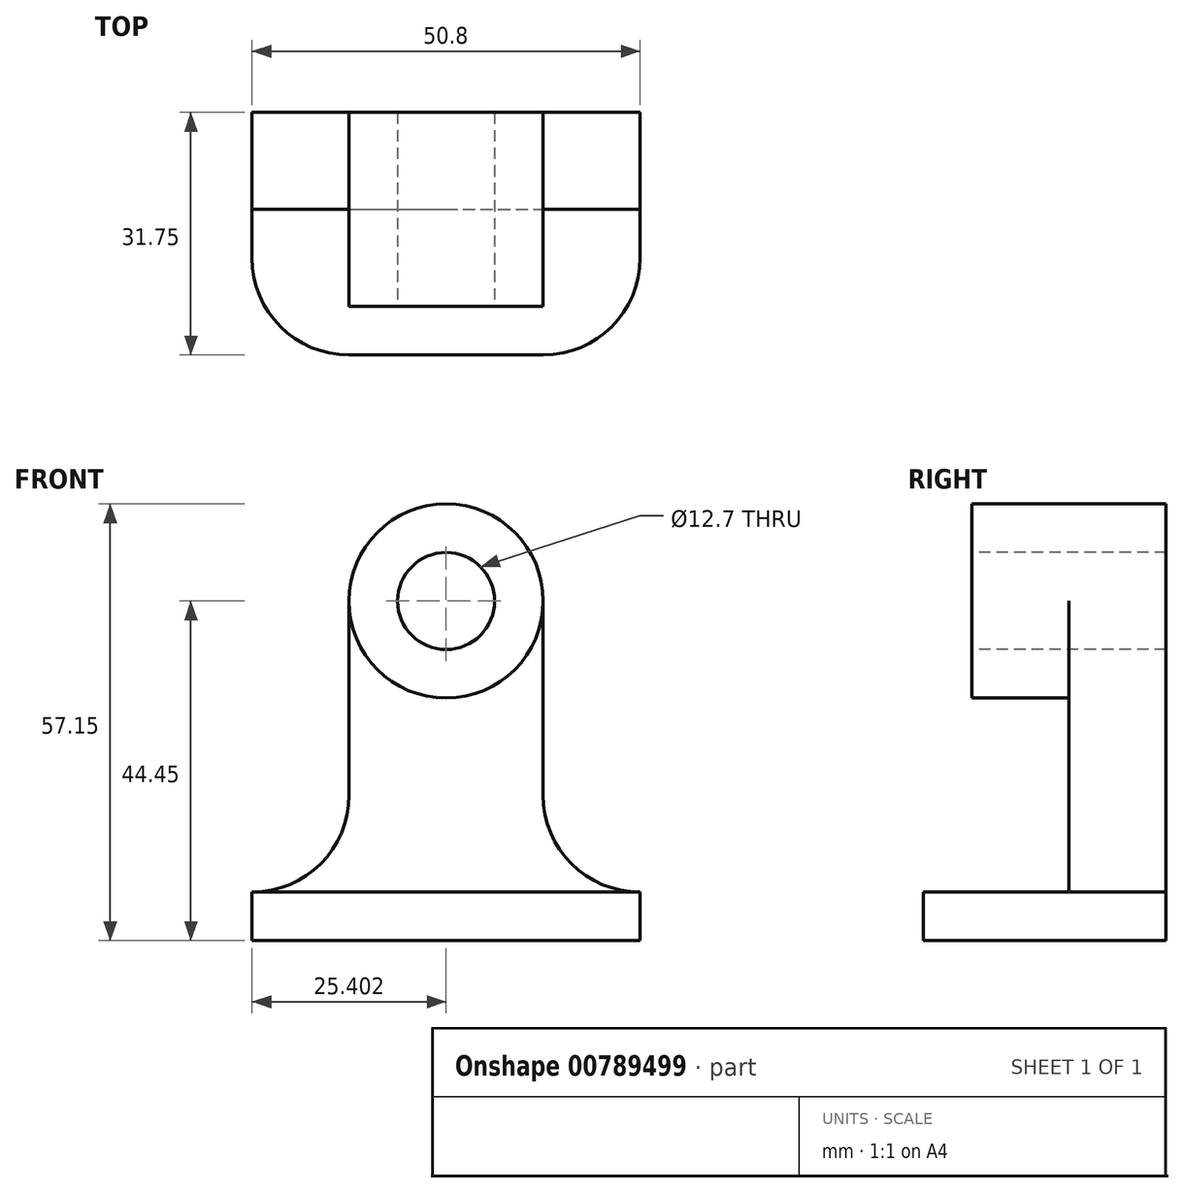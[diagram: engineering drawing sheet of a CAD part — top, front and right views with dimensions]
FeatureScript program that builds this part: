
annotation { "Feature Type Name" : "Feature", "Feature Type Description" : "" }
export const myFeature = defineFeature(function(context is Context, id is Id, definition is map)
    precondition{}
    {
        {
            var Q0;
            Q0=qCreatedBy(makeId("Front.planeOp"),FACE);
            var sketch = newSketch(context, id + "F0", { "sketchPlane" : qUnion([Q0])});
            skLineSegment(sketch, "E0", {"start": v(-22.4, 6.35) * mm, "end": v(-22.4, 0) * mm});
            skLineSegment(sketch, "E1", {"start": v(-22.4, 0) * mm, "end": v(28.4, 0) * mm});
            skLineSegment(sketch, "E2", {"start": v(28.4, 0) * mm, "end": v(28.4, 6.35) * mm});
            skLineSegment(sketch, "E3", {"start": v(28.4, 6.35) * mm, "end": v(15.7, 6.35) * mm});
            skLineSegment(sketch, "E4", {"start": v(-22.4, 6.35) * mm, "end": v(-9.7, 6.35) * mm});
            skLineSegment(sketch, "E5", {"start": v(-9.7, 6.35) * mm, "end": v(-9.7, 57.15) * mm});
            skLineSegment(sketch, "E6", {"start": v(15.7, 6.35) * mm, "end": v(15.7, 57.15) * mm});
            skLineSegment(sketch, "E7", {"start": v(15.7, 57.15) * mm, "end": v(-9.7, 57.15) * mm});
            skSolve(sketch);
        }
        {
            var Q0;
            Q0=makeQuery(id+"F0.imprint","IMPRINT",FACE,{"disambiguationData":[TD([[makeQuery(id+"F0.imprint","IMPRINT",EDGE,{"derivedFrom":sQuery(id+"F0.wireOp",EDGE,"E0")}),1.0]])]});
            extrude(context, id + "F1", {"entities" : qUnion([Q0]), "depth" : 31.75 * mm, "offsetDistance" : 25.4 * mm});
        }
        {
            var Q0;
            Q0=makeQuery(id+"F1.opExtrude","CAP_FACE",FACE,{"disambiguationData":[OSD([sQuery(id+"F0.wireOp",EDGE,"E0"),sQuery(id+"F0.wireOp",EDGE,"E1"),sQuery(id+"F0.wireOp",EDGE,"E2"),sQuery(id+"F0.wireOp",EDGE,"E3"),sQuery(id+"F0.wireOp",EDGE,"E4"),sQuery(id+"F0.wireOp",EDGE,"E5"),sQuery(id+"F0.wireOp",EDGE,"E6"),sQuery(id+"F0.wireOp",EDGE,"E7")])],"isStart":false});
            var sketch = newSketch(context, id + "F2", { "sketchPlane" : qUnion([Q0])});
            skCircle(sketch, "E8", {"center": v(3, 44.45) * mm, "radius": 6.35 * mm});
            skSolve(sketch);
        }
        {
            var Q0;
            Q0=makeQuery(id+"F2.imprint","IMPRINT",FACE,{"disambiguationData":[TD([[makeQuery(id+"F2.imprint","IMPRINT",EDGE,{"derivedFrom":sQuery(id+"F2.wireOp",EDGE,"E8")}),1.0]])]});
            var Q1;
            Q1 = qSketchRegion(id + "F4", true);
            extrude(context, id + "F3", {"entities" : qUnion([Q0, Q1]), "operationType" : NewBodyOperationType.REMOVE, "oppositeDirection" : true, "depth" : 31.75 * mm, "offsetDistance" : 25.4 * mm});
        }
        {
            var Q0;
            Q0=makeQuery(id+"F1.opExtrude","CAP_FACE",FACE,{"disambiguationData":[OSD([sQuery(id+"F0.wireOp",EDGE,"E0"),sQuery(id+"F0.wireOp",EDGE,"E1"),sQuery(id+"F0.wireOp",EDGE,"E2"),sQuery(id+"F0.wireOp",EDGE,"E3"),sQuery(id+"F0.wireOp",EDGE,"E4"),sQuery(id+"F0.wireOp",EDGE,"E5"),sQuery(id+"F0.wireOp",EDGE,"E6"),sQuery(id+"F0.wireOp",EDGE,"E7")])],"isStart":false});
            var sketch = newSketch(context, id + "F4", { "sketchPlane" : qUnion([Q0])});
            skCircle(sketch, "E9", {"center": v(3, 44.45) * mm, "radius": 12.7 * mm});
            skSolve(sketch);
        }
        {
            var Q0;
            {var subQ0=sQuery(id+"F4.wireOp",EDGE,"E9");var subQ1=makeQuery(id+"F1.opExtrude","CAP_EDGE",EDGE,{"disambiguationData":[OSD([sQuery(id+"F0.wireOp",EDGE,"E7")])],"isStart":false});var subQ2=makeQuery(id+"F4.imprint","INTERSECT",VERTEX,{"derivedFrom":[subQ1,subQ0]});Q0=makeQuery(id+"F4.imprint","IMPRINT",FACE,{"disambiguationData":[TD([[makeQuery(id+"F4.imprint","IMPRINT",EDGE,{"disambiguationData":[TD([[subQ2,-1.0]])],"derivedFrom":subQ0}),-1.0]])]});}
            var Q1;
            {var subQ0=sQuery(id+"F4.wireOp",EDGE,"E9");var subQ1=makeQuery(id+"F1.opExtrude","CAP_EDGE",EDGE,{"disambiguationData":[OSD([sQuery(id+"F0.wireOp",EDGE,"E7")])],"isStart":false});var subQ2=makeQuery(id+"F4.imprint","INTERSECT",VERTEX,{"derivedFrom":[subQ1,subQ0]});Q1=makeQuery(id+"F4.imprint","IMPRINT",FACE,{"disambiguationData":[TD([[makeQuery(id+"F4.imprint","IMPRINT",EDGE,{"disambiguationData":[TD([[subQ2,1.0]])],"derivedFrom":subQ0}),-1.0]])]});}
            extrude(context, id + "F5", {"entities" : qUnion([Q0, Q1]), "operationType" : NewBodyOperationType.REMOVE, "oppositeDirection" : true, "depth" : 31.75 * mm, "offsetDistance" : 25.4 * mm});
        }
        {
            var Q0;
            Q0=makeQuery(id+"F1.opExtrude","CAP_FACE",FACE,{"disambiguationData":[OSD([sQuery(id+"F0.wireOp",EDGE,"E0"),sQuery(id+"F0.wireOp",EDGE,"E1"),sQuery(id+"F0.wireOp",EDGE,"E2"),sQuery(id+"F0.wireOp",EDGE,"E3"),sQuery(id+"F0.wireOp",EDGE,"E4"),sQuery(id+"F0.wireOp",EDGE,"E5"),sQuery(id+"F0.wireOp",EDGE,"E6"),sQuery(id+"F0.wireOp",EDGE,"E7")])],"isStart":false});
            var sketch = newSketch(context, id + "F6", { "sketchPlane" : qUnion([Q0])});
            skCircle(sketch, "E10", {"center": v(3, 44.45) * mm, "radius": 12.7 * mm});
            skLineSegment(sketch, "E11", {"start": v(-9.7, 6.35) * mm, "end": v(15.7, 6.35) * mm});
            skSolve(sketch);
        }
        {
            var Q0;
            Q0=makeQuery(id+"F6.imprint","IMPRINT",FACE,{"disambiguationData":[TD([[makeQuery(id+"F6.imprint","IMPRINT",EDGE,{"derivedFrom":sQuery(id+"F6.wireOp",EDGE,"E11")}),1.0]])]});
            extrude(context, id + "F7", {"entities" : qUnion([Q0]), "operationType" : NewBodyOperationType.REMOVE, "oppositeDirection" : true, "depth" : 19.05 * mm, "offsetDistance" : 25.4 * mm});
        }
        {
            var Q0;
            {var subQ1=sQuery(id+"F0.wireOp",EDGE,"E7");var subQ3=sQuery(id+"F0.wireOp",EDGE,"E5");var subQ4=sQuery(id+"F0.wireOp",EDGE,"E6");Q0=makeQuery(id+"F7.boolean.opBoolean","SPLIT",FACE,{"disambiguationData":[TD([makeQuery(id+"F3.boolean.opBoolean","COPY",FACE,{"derivedFrom":makeQuery(id+"F3.opExtrude","SWEPT_FACE",FACE,{"disambiguationData":[OSD([sQuery(id+"F2.wireOp",EDGE,"E8")])]})})])],"derivedFrom":makeQuery(id+"F1.opExtrude","CAP_FACE",FACE,{"disambiguationData":[OSD([sQuery(id+"F0.wireOp",EDGE,"E0"),sQuery(id+"F0.wireOp",EDGE,"E1"),sQuery(id+"F0.wireOp",EDGE,"E2"),sQuery(id+"F0.wireOp",EDGE,"E3"),sQuery(id+"F0.wireOp",EDGE,"E4"),subQ3,subQ4,subQ1])],"isStart":false})});}
            extrude(context, id + "F8", {"entities" : qUnion([Q0]), "operationType" : NewBodyOperationType.REMOVE, "oppositeDirection" : true, "depth" : 6.35 * mm, "offsetDistance" : 25.4 * mm});
        }
        {
            var Q0;
            {var subQ0=sQuery(id+"F0.wireOp",EDGE,"E2");var subQ1=sQuery(id+"F0.wireOp",EDGE,"E1");var subQ2=sQuery(id+"F0.wireOp",EDGE,"E3");var subQ3=sQuery(id+"F0.wireOp",EDGE,"E0");var subQ4=sQuery(id+"F0.wireOp",EDGE,"E4");Q0=makeQuery(id+"F7.boolean.opBoolean","SPLIT",FACE,{"disambiguationData":[TD([makeQuery(id+"F1.opExtrude","SWEPT_FACE",FACE,{"disambiguationData":[OSD([subQ3])]})])],"derivedFrom":makeQuery(id+"F1.opExtrude","CAP_FACE",FACE,{"disambiguationData":[OSD([subQ3,subQ1,subQ0,subQ2,subQ4,sQuery(id+"F0.wireOp",EDGE,"E5"),sQuery(id+"F0.wireOp",EDGE,"E6"),sQuery(id+"F0.wireOp",EDGE,"E7")])],"isStart":false})});}
            var sketch = newSketch(context, id + "F9", { "sketchPlane" : qUnion([Q0])});
            skLineSegment(sketch, "E12", {"start": v(-22.4, 6.35) * mm, "end": v(-22.4, 19.05) * mm});
            skLineSegment(sketch, "E13", {"start": v(-22.4, 19.05) * mm, "end": v(-9.7, 19.05) * mm});
            skLineSegment(sketch, "E14", {"start": v(-9.7, 19.05) * mm, "end": v(-9.7, 6.35) * mm});
            skLineSegment(sketch, "E15", {"start": v(-9.7, 6.35) * mm, "end": v(-22.4, 6.35) * mm});
            skSolve(sketch);
        }
        {
            var Q0;
            Q0=makeQuery(id+"F9.imprint","IMPRINT",FACE,{"disambiguationData":[TD([[makeQuery(id+"F9.imprint","IMPRINT",EDGE,{"derivedFrom":sQuery(id+"F9.wireOp",EDGE,"E12")}),-1.0]])]});
            extrude(context, id + "F10", {"entities" : qUnion([Q0]), "operationType" : NewBodyOperationType.ADD, "oppositeDirection" : true, "depth" : 31.75 * mm, "offsetDistance" : 25.4 * mm});
        }
        {
            var Q0;
            {var subQ0=sQuery(id+"F0.wireOp",EDGE,"E2");var subQ1=sQuery(id+"F0.wireOp",EDGE,"E1");var subQ2=sQuery(id+"F0.wireOp",EDGE,"E3");var subQ3=sQuery(id+"F0.wireOp",EDGE,"E0");var subQ4=sQuery(id+"F0.wireOp",EDGE,"E4");Q0=makeQuery(id+"F10.boolean.opBoolean","MERGE",FACE,{"derivedFrom":[makeQuery(id+"F7.boolean.opBoolean","SPLIT",FACE,{"disambiguationData":[TD([makeQuery(id+"F1.opExtrude","SWEPT_FACE",FACE,{"disambiguationData":[OSD([subQ3])]})])],"derivedFrom":makeQuery(id+"F1.opExtrude","CAP_FACE",FACE,{"disambiguationData":[OSD([subQ3,subQ1,subQ0,subQ2,subQ4,sQuery(id+"F0.wireOp",EDGE,"E5"),sQuery(id+"F0.wireOp",EDGE,"E6"),sQuery(id+"F0.wireOp",EDGE,"E7")])],"isStart":false})}),makeQuery(id+"F10.opExtrude","CAP_FACE",FACE,{"disambiguationData":[OSD([sQuery(id+"F9.wireOp",EDGE,"E12"),sQuery(id+"F9.wireOp",EDGE,"E13"),sQuery(id+"F9.wireOp",EDGE,"E14"),sQuery(id+"F9.wireOp",EDGE,"E15")])],"isStart":true})]});}
            var sketch = newSketch(context, id + "F11", { "sketchPlane" : qUnion([Q0])});
            skLineSegment(sketch, "E16", {"start": v(-9.7, 6.35) * mm, "end": v(-22.4, 6.35) * mm});
            skLineSegment(sketch, "E17", {"start": v(-22.4, 6.35) * mm, "end": v(-22.4, 19.05) * mm});
            skLineSegment(sketch, "E18", {"start": v(-22.4, 19.05) * mm, "end": v(-9.7, 19.05) * mm});
            skLineSegment(sketch, "E19", {"start": v(-9.7, 19.05) * mm, "end": v(-9.7, 6.35) * mm});
            skSolve(sketch);
        }
        {
            var Q0;
            Q0=makeQuery(id+"F11.imprint","IMPRINT",FACE,{"disambiguationData":[TD([[makeQuery(id+"F11.imprint","IMPRINT",EDGE,{"derivedFrom":sQuery(id+"F11.wireOp",EDGE,"E16")}),-1.0]])]});
            extrude(context, id + "F12", {"entities" : qUnion([Q0]), "operationType" : NewBodyOperationType.REMOVE, "oppositeDirection" : true, "depth" : 19.05 * mm, "offsetDistance" : 25.4 * mm});
        }
        {
            var Q0;
            Q0=makeQuery(id+"F12.boolean.opBoolean","MERGE",FACE,{"derivedFrom":[makeQuery(id+"F7.boolean.opBoolean","COPY",FACE,{"derivedFrom":makeQuery(id+"F7.opExtrude","CAP_FACE",FACE,{"disambiguationData":[OSD([sQuery(id+"F0.wireOp",EDGE,"E5"),sQuery(id+"F0.wireOp",EDGE,"E6"),sQuery(id+"F6.wireOp",EDGE,"E10"),sQuery(id+"F6.wireOp",EDGE,"E11")])],"isStart":false})}),makeQuery(id+"F12.opExtrude","CAP_FACE",FACE,{"disambiguationData":[OSD([sQuery(id+"F11.wireOp",EDGE,"E16"),sQuery(id+"F11.wireOp",EDGE,"E17"),sQuery(id+"F11.wireOp",EDGE,"E18"),sQuery(id+"F11.wireOp",EDGE,"E19")])],"isStart":false})]});
            var sketch = newSketch(context, id + "F13", { "sketchPlane" : qUnion([Q0])});
            skArc(sketch, "E20", {"start": v(-22.4, 6.35) * mm, "mid": v(-13.42, 10.07) * mm, "end": v(-9.7, 19.05) * mm});
            skSolve(sketch);
        }
        {
            var Q0;
            Q0=makeQuery(id+"F13.imprint","IMPRINT",FACE,{"disambiguationData":[TD([[makeQuery(id+"F13.imprint","IMPRINT",EDGE,{"derivedFrom":sQuery(id+"F13.wireOp",EDGE,"E20")}),1.0]])]});
            extrude(context, id + "F14", {"entities" : qUnion([Q0]), "operationType" : NewBodyOperationType.REMOVE, "oppositeDirection" : true, "depth" : 12.7 * mm});
        }
        {
            var Q0;
            Q0=makeQuery(id+"F12.boolean.opBoolean","MERGE",FACE,{"derivedFrom":[makeQuery(id+"F7.boolean.opBoolean","COPY",FACE,{"derivedFrom":makeQuery(id+"F7.opExtrude","CAP_FACE",FACE,{"disambiguationData":[OSD([sQuery(id+"F0.wireOp",EDGE,"E5"),sQuery(id+"F0.wireOp",EDGE,"E6"),sQuery(id+"F6.wireOp",EDGE,"E10"),sQuery(id+"F6.wireOp",EDGE,"E11")])],"isStart":false})}),makeQuery(id+"F12.opExtrude","CAP_FACE",FACE,{"disambiguationData":[OSD([sQuery(id+"F11.wireOp",EDGE,"E16"),sQuery(id+"F11.wireOp",EDGE,"E17"),sQuery(id+"F11.wireOp",EDGE,"E18"),sQuery(id+"F11.wireOp",EDGE,"E19")])],"isStart":false})]});
            var sketch = newSketch(context, id + "F15", { "sketchPlane" : qUnion([Q0])});
            skLineSegment(sketch, "E21", {"start": v(15.7, 6.35) * mm, "end": v(15.7, 19.05) * mm});
            skLineSegment(sketch, "E22", {"start": v(15.7, 6.35) * mm, "end": v(28.4, 6.35) * mm});
            skLineSegment(sketch, "E23", {"start": v(28.4, 6.35) * mm, "end": v(28.4, 19.05) * mm});
            skLineSegment(sketch, "E24", {"start": v(28.4, 19.05) * mm, "end": v(15.7, 19.05) * mm});
            skSolve(sketch);
        }
        {
            var Q0;
            Q0=makeQuery(id+"F15.imprint","IMPRINT",FACE,{"disambiguationData":[TD([[makeQuery(id+"F15.imprint","IMPRINT",EDGE,{"derivedFrom":sQuery(id+"F15.wireOp",EDGE,"E21")}),-1.0]])]});
            extrude(context, id + "F16", {"entities" : qUnion([Q0]), "operationType" : NewBodyOperationType.ADD, "oppositeDirection" : true, "depth" : 12.7 * mm});
        }
        {
            var Q0;
            Q0=makeQuery(id+"F16.boolean.opBoolean","MERGE",FACE,{"derivedFrom":[makeQuery(id+"F12.boolean.opBoolean","MERGE",FACE,{"derivedFrom":[makeQuery(id+"F7.boolean.opBoolean","COPY",FACE,{"derivedFrom":makeQuery(id+"F7.opExtrude","CAP_FACE",FACE,{"disambiguationData":[OSD([sQuery(id+"F0.wireOp",EDGE,"E5"),sQuery(id+"F0.wireOp",EDGE,"E6"),sQuery(id+"F6.wireOp",EDGE,"E10"),sQuery(id+"F6.wireOp",EDGE,"E11")])],"isStart":false})}),makeQuery(id+"F12.opExtrude","CAP_FACE",FACE,{"disambiguationData":[OSD([sQuery(id+"F11.wireOp",EDGE,"E16"),sQuery(id+"F11.wireOp",EDGE,"E17"),sQuery(id+"F11.wireOp",EDGE,"E18"),sQuery(id+"F11.wireOp",EDGE,"E19")])],"isStart":false})]}),makeQuery(id+"F16.opExtrude","CAP_FACE",FACE,{"disambiguationData":[OSD([sQuery(id+"F15.wireOp",EDGE,"E21"),sQuery(id+"F15.wireOp",EDGE,"E22"),sQuery(id+"F15.wireOp",EDGE,"E23"),sQuery(id+"F15.wireOp",EDGE,"E24")])],"isStart":true})]});
            var sketch = newSketch(context, id + "F17", { "sketchPlane" : qUnion([Q0])});
            skArc(sketch, "E25", {"start": v(15.7, 19.05) * mm, "mid": v(19.42, 10.07) * mm, "end": v(28.4, 6.35) * mm});
            skSolve(sketch);
        }
        {
            var Q0;
            Q0=makeQuery(id+"F17.imprint","IMPRINT",FACE,{"disambiguationData":[TD([[makeQuery(id+"F17.imprint","IMPRINT",EDGE,{"derivedFrom":sQuery(id+"F17.wireOp",EDGE,"E25")}),1.0]])]});
            extrude(context, id + "F18", {"entities" : qUnion([Q0]), "operationType" : NewBodyOperationType.REMOVE, "oppositeDirection" : true, "depth" : 12.7 * mm, "offsetDistance" : 25.4 * mm});
        }
        {
            var Q0;
            Q0=qCreatedBy(makeId("Top.planeOp"),FACE);
            var sketch = newSketch(context, id + "F19", { "sketchPlane" : qUnion([Q0])});
            skCircle(sketch, "E26", {"center": v(-12.87, -22.23) * mm, "radius": 1.59 * mm});
            skCircle(sketch, "E27", {"center": v(18.88, -22.23) * mm, "radius": 1.59 * mm});
            skSolve(sketch);
        }
        {
            var Q0;
            Q0=makeQuery(id+"F19.imprint","IMPRINT",FACE,{"disambiguationData":[TD([[makeQuery(id+"F19.imprint","IMPRINT",EDGE,{"derivedFrom":sQuery(id+"F19.wireOp",EDGE,"E26")}),1.0]])]});
            var Q1;
            Q1=makeQuery(id+"F19.imprint","IMPRINT",FACE,{"disambiguationData":[TD([[makeQuery(id+"F19.imprint","IMPRINT",EDGE,{"derivedFrom":sQuery(id+"F19.wireOp",EDGE,"E27")}),1.0]])]});
            extrude(context, id + "F20", {"entities" : qUnion([Q0, Q1]), "operationType" : NewBodyOperationType.REMOVE, "oppositeDirection" : true, "depth" : 12.7 * mm});
        }
        {
            var Q0;
            Q0=makeQuery(id+"F12.boolean.opBoolean","MERGE",FACE,{"derivedFrom":[makeQuery(id+"F7.boolean.opBoolean","MERGE",FACE,{"derivedFrom":[makeQuery(id+"F1.opExtrude","SWEPT_FACE",FACE,{"disambiguationData":[OSD([sQuery(id+"F0.wireOp",EDGE,"E3")])]}),makeQuery(id+"F1.opExtrude","SWEPT_FACE",FACE,{"disambiguationData":[OSD([sQuery(id+"F0.wireOp",EDGE,"E4")])]}),makeQuery(id+"F7.opExtrude","SWEPT_FACE",FACE,{"disambiguationData":[OSD([sQuery(id+"F6.wireOp",EDGE,"E11")])]})]}),makeQuery(id+"F12.opExtrude","SWEPT_FACE",FACE,{"disambiguationData":[OSD([sQuery(id+"F11.wireOp",EDGE,"E16")])]})]});
            var sketch = newSketch(context, id + "F21", { "sketchPlane" : qUnion([Q0])});
            skArc(sketch, "E28", {"start": v(-22.4, -19.05) * mm, "mid": v(-18.68, -28.03) * mm, "end": v(-9.7, -31.75) * mm});
            skArc(sketch, "E29", {"start": v(15.7, -31.75) * mm, "mid": v(24.68, -28.03) * mm, "end": v(28.4, -19.05) * mm});
            skSolve(sketch);
        }
        {
            var Q0;
            {var subQ0=sQuery(id+"F21.wireOp",EDGE,"E28");Q0=makeQuery(id+"F21.imprint","IMPRINT",FACE,{"disambiguationData":[TD([[makeQuery(id+"F21.imprint","IMPRINT",EDGE,{"derivedFrom":subQ0}),-1.0]])]});}
            var Q1;
            {var subQ0=sQuery(id+"F21.wireOp",EDGE,"E29");Q1=makeQuery(id+"F21.imprint","IMPRINT",FACE,{"disambiguationData":[TD([[makeQuery(id+"F21.imprint","IMPRINT",EDGE,{"derivedFrom":subQ0}),-1.0]])]});}
            extrude(context, id + "F22", {"entities" : qUnion([Q0, Q1]), "operationType" : NewBodyOperationType.REMOVE, "oppositeDirection" : true, "depth" : 6.35 * mm});
        }
    });
